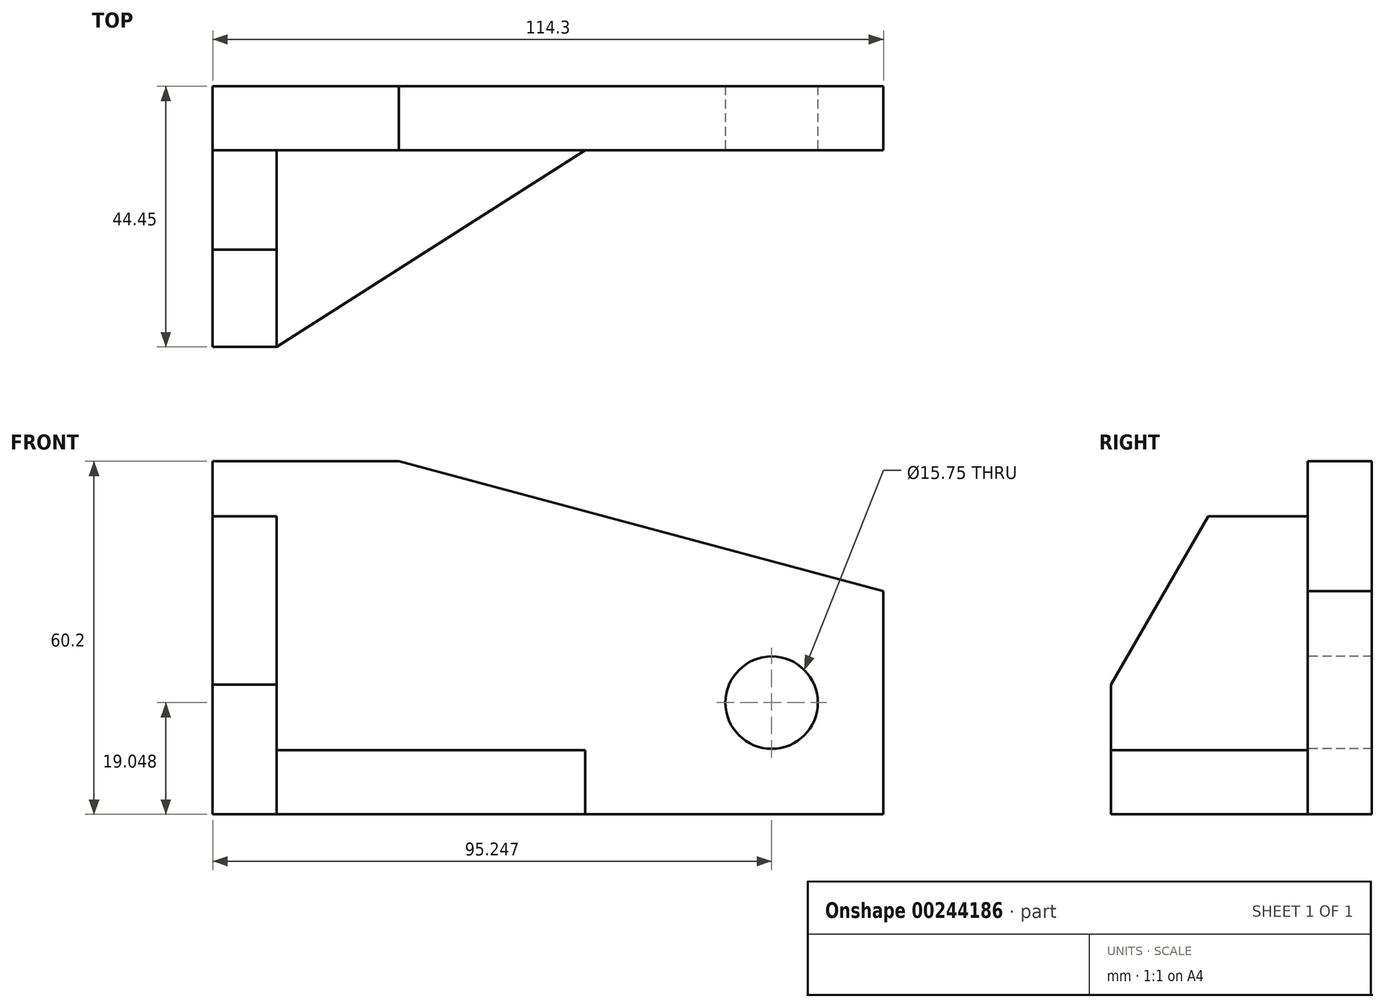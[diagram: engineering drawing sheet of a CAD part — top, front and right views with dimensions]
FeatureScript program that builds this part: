
annotation { "Feature Type Name" : "Feature", "Feature Type Description" : "" }
export const myFeature = defineFeature(function(context is Context, id is Id, definition is map)
    precondition{}
    {
        {
            var Q0;
            Q0=qCreatedBy(makeId("Front.planeOp"),FACE);
            var sketch = newSketch(context, id + "F0", { "sketchPlane" : qUnion([Q0])});
            skLineSegment(sketch, "E0.bottom", {"start": v(-57.43, 29.76) * mm, "end": v(-25.68, 29.76) * mm});
            skLineSegment(sketch, "E0.top", {"start": v(-57.43, -30.44) * mm, "end": v(56.87, -30.44) * mm});
            skLineSegment(sketch, "E0.left", {"start": v(-57.43, 29.76) * mm, "end": v(-57.43, -30.44) * mm});
            skLineSegment(sketch, "E0.right", {"start": v(56.87, 7.64) * mm, "end": v(56.87, -30.44) * mm});
            skLineSegment(sketch, "E1", {"start": v(-25.68, 29.76) * mm, "end": v(56.87, 7.64) * mm});
            skSolve(sketch);
        }
        {
            var Q0;
            Q0 = qSketchRegion(id + "F0", true);
            extrude(context, id + "F1", {"entities" : qUnion([Q0]), "depth" : 10.92 * mm});
        }
        {
            var Q0;
            Q0=makeQuery(id+"F1.opExtrude","CAP_FACE",FACE,{"disambiguationData":[OSD([sQuery(id+"F0.wireOp",EDGE,"E0.bottom"),sQuery(id+"F0.wireOp",EDGE,"E0.top"),sQuery(id+"F0.wireOp",EDGE,"E0.left"),sQuery(id+"F0.wireOp",EDGE,"E0.right"),sQuery(id+"F0.wireOp",EDGE,"E1")])],"isStart":false});
            var sketch = newSketch(context, id + "F2", { "sketchPlane" : qUnion([Q0])});
            skLineSegment(sketch, "E2.bottom", {"start": v(-57.43, -30.44) * mm, "end": v(-46.51, -30.44) * mm});
            skLineSegment(sketch, "E2.top", {"start": v(-57.43, 20.36) * mm, "end": v(-46.51, 20.36) * mm});
            skLineSegment(sketch, "E2.left", {"start": v(-57.43, -30.44) * mm, "end": v(-57.43, 20.36) * mm});
            skLineSegment(sketch, "E2.right", {"start": v(-46.51, -30.44) * mm, "end": v(-46.51, 20.36) * mm});
            skSolve(sketch);
        }
        {
            var Q0;
            Q0 = qSketchRegion(id + "F2", true);
            extrude(context, id + "F3", {"entities" : qUnion([Q0]), "operationType" : NewBodyOperationType.ADD, "depth" : 33.53 * mm});
        }
        {
            var Q0;
            Q0=makeQuery(id+"F3.opExtrude","SWEPT_FACE",FACE,{"disambiguationData":[OSD([sQuery(id+"F2.wireOp",EDGE,"E2.right")])]});
            var sketch = newSketch(context, id + "F4", { "sketchPlane" : qUnion([Q0])});
            skLineSegment(sketch, "E3", {"start": v(-44.45, -8.34) * mm, "end": v(-27.88, 20.36) * mm});
            skSolve(sketch);
        }
        {
            var Q0;
            {var subQ0=sQuery(id+"F4.wireOp",EDGE,"TrvoHkB6-jBkV-KDAm-jMnS-FOYwTlfdgzAm");Q0=makeQuery(id+"F4.imprint","IMPRINT",FACE,{"disambiguationData":[TD([[makeQuery(id+"F4.imprint","IMPRINT",EDGE,{"derivedFrom":subQ0}),1.0]])]});}
            var Q1;
            {var subQ0=sQuery(id+"F4.wireOp",EDGE,"E3");Q1=makeQuery(id+"F4.imprint","IMPRINT",FACE,{"disambiguationData":[TD([[makeQuery(id+"F4.imprint","IMPRINT",EDGE,{"derivedFrom":subQ0}),1.0]])]});}
            extrude(context, id + "F5", {"entities" : qUnion([Q0, Q1]), "operationType" : NewBodyOperationType.REMOVE, "endBound" : BoundingType.THROUGH_ALL, "oppositeDirection" : true, "depth" : 25.4 * mm});
        }
        {
            var Q0;
            Q0=makeQuery(id+"F3.opExtrude","SWEPT_FACE",FACE,{"disambiguationData":[OSD([sQuery(id+"F2.wireOp",EDGE,"E2.right")])]});
            var sketch = newSketch(context, id + "F6", { "sketchPlane" : qUnion([Q0])});
            skLineSegment(sketch, "E4.bottom", {"start": v(-44.45, -30.44) * mm, "end": v(-10.92, -30.44) * mm});
            skLineSegment(sketch, "E4.top", {"start": v(-44.45, -19.52) * mm, "end": v(-10.92, -19.52) * mm});
            skLineSegment(sketch, "E4.left", {"start": v(-44.45, -30.44) * mm, "end": v(-44.45, -19.52) * mm});
            skLineSegment(sketch, "E4.right", {"start": v(-10.92, -30.44) * mm, "end": v(-10.92, -19.52) * mm});
            skSolve(sketch);
        }
        {
            var Q0;
            Q0 = qSketchRegion(id + "F6", true);
            extrude(context, id + "F7", {"entities" : qUnion([Q0]), "operationType" : NewBodyOperationType.ADD, "depth" : 52.58 * mm});
        }
        {
            var Q0;
            Q0=makeQuery(id+"F7.opExtrude","SWEPT_FACE",FACE,{"disambiguationData":[OSD([sQuery(id+"F6.wireOp",EDGE,"E4.top")])]});
            var sketch = newSketch(context, id + "F8", { "sketchPlane" : qUnion([Q0])});
            skLineSegment(sketch, "E5", {"start": v(-46.51, -44.45) * mm, "end": v(6.07, -10.92) * mm});
            skSolve(sketch);
        }
        {
            var Q0;
            Q0 = qSketchRegion(id + "F8", true);
            var Q1;
            Q1=makeQuery(id+"F8.imprint","IMPRINT",FACE,{"disambiguationData":[TD([[makeQuery(id+"F8.imprint","IMPRINT",EDGE,{"derivedFrom":sQuery(id+"F8.wireOp",EDGE,"E5")}),-1.0]])]});
            extrude(context, id + "F9", {"entities" : qUnion([Q0, Q1]), "operationType" : NewBodyOperationType.REMOVE, "endBound" : BoundingType.THROUGH_ALL, "oppositeDirection" : true, "depth" : 25.4 * mm});
        }
        {
            var Q0;
            Q0=makeQuery(id+"F1.opExtrude","CAP_FACE",FACE,{"disambiguationData":[OSD([sQuery(id+"F0.wireOp",EDGE,"E0.bottom"),sQuery(id+"F0.wireOp",EDGE,"E0.top"),sQuery(id+"F0.wireOp",EDGE,"E0.left"),sQuery(id+"F0.wireOp",EDGE,"E0.right"),sQuery(id+"F0.wireOp",EDGE,"E1")])],"isStart":false});
            var sketch = newSketch(context, id + "F10", { "sketchPlane" : qUnion([Q0])});
            skCircle(sketch, "E6", {"center": v(37.82, -11.4) * mm, "radius": 7.87 * mm});
            skSolve(sketch);
        }
        {
            var Q0;
            Q0=sQuery(id+"F10.wireOp",VERTEX,"E6.center");
            var Q1;
            Q1=makeQuery(id+"F1.opExtrude","SWEPT_BODY",BODY,{"disambiguationData":[OSD([sQuery(id+"F0.wireOp",EDGE,"E0.bottom"),sQuery(id+"F0.wireOp",EDGE,"E0.top"),sQuery(id+"F0.wireOp",EDGE,"E0.left"),sQuery(id+"F0.wireOp",EDGE,"E0.right"),sQuery(id+"F0.wireOp",EDGE,"E1")])]});
            hole(context, id + "F11", {"style" : HoleStyle.SIMPLE, "endStyle" : HoleEndStyle.THROUGH, "holeDiameter" : 15.75 * mm, "locations" : qUnion([Q0]), "scope" : qUnion([Q1]), "isTappedThrough" : true});
        }
    });
